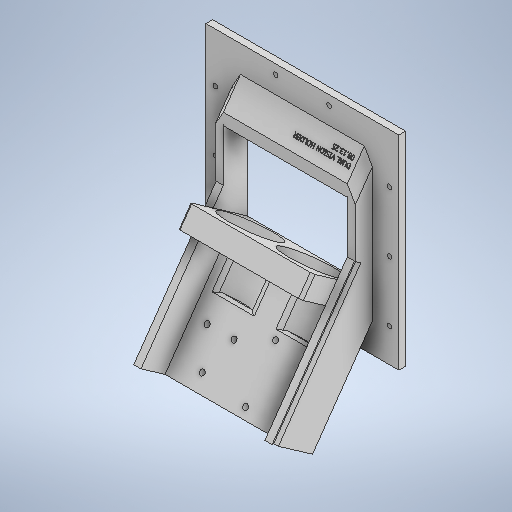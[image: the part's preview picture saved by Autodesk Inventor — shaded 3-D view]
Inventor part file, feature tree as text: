
AUTODESK INVENTOR PART (.ipt)
format: ipt  version: 2025.3 (Build 293356030, 356C)  size: 1,616,896 bytes
history: native  units: in
note: dims shown in document units (in); Inventor stores cm internally (conversion verified against a paired STEP export)
features: sketch x58, extrude x53, projected_geometry x13, plane x5, chamfer x3, move_body x1, hole x1
ambient origin geometry x8: Origin, YZ Plane, XZ Plane, XY Plane, X Axis, Y Axis, Z Axis, Center Point
bodies: Solid1 (feature_tree)
feature tree (134):
  extrude  "Extrusion1"  Depth=0.1969in TaperAngle=0.0deg
  move_body  "Move Body1"
  plane  "Work Plane1"
  sketch  "Sketch5"  dims[d5=1.7717in d6=1.7717in d7=1.7717in d8=1.7717in d9=0.8108in d10=90.0deg d11=0.0787in d12=0.3701in d13=0.4252in d14=0.1362in d15=-0.0984in d16=-0.0591in d17=0.0in]
  plane  "Work Plane2"
  extrude  "Extrusion4"  TaperAngle=0.0deg  [1 undecoded]
  extrude  "Extrusion6"  Depth=0.2405in
  extrude  "Extrusion8"  Depth=2.7559in TaperAngle=0.0deg
  chamfer  "Chamfer1"  [1 undecoded]
  extrude  "Extrusion11"  Depth=0.2362in
  plane  "Work Plane3"
  extrude  "Extrusion13"  Depth=0.1969in TaperAngle=0.0deg
  plane  "Work Plane4"
  plane  "Work Plane6"
  extrude  "Extrusion21"  Depth=0.5027in
  extrude  "Extrusion22"  Depth=0.5027in
  extrude  "Extrusion25"  Depth=1.1811in TaperAngle=0.0deg
  extrude  "Extrusion26"  Depth=0.1969in
  sketch  "Sketch33"  dims[d100=3.6403in d101=2.7717in]
  extrude  "Extrusion27"  Depth=0.2362in TaperAngle=0.0deg
  extrude  "Extrusion29"  Depth=3.6403in
  extrude  "Extrusion28"  Depth=0.6299in TaperAngle=0.0deg
  sketch  "Sketch36"  dims[d124=0.9712in d125=0.0in d126=0.5906in d127=0.0in]
  extrude  "Extrusion30"  Depth=0.7874in
  extrude  "Extrusion31"  Depth=0.5906in TaperAngle=0.0deg
  sketch  "Sketch39"  dims[d164=0.1181in d165=0.0in d168=0.5906in d169=0.0in]
  extrude  "Extrusion35"  Depth=11.3469in TaperAngle=0.0deg
  sketch  "Sketch45"  dims[d176=0.7313in d177=0.0in d186=0.0in d187=0.0in]
  extrude  "Extrusion37"  Depth=0.1181in TaperAngle=0.0deg
  extrude  "Extrusion38"  Depth=0.1181in TaperAngle=0.0deg
  extrude  "Extrusion40"  TaperAngle=0.0deg  [1 undecoded]
  extrude  "Extrusion41"  TaperAngle=0.0deg  [1 undecoded]
  extrude  "Extrusion43"  TaperAngle=0.0deg  [1 undecoded]
  extrude  "Extrusion44"  Depth=0.0394in TaperAngle=0.0deg
  extrude  "Extrusion46"  Depth=3.9671in TaperAngle=0.0deg
  extrude  "Extrusion47"  Depth=0.1969in
  extrude  "Extrusion48"  TaperAngle=60.0deg  [1 undecoded]
  sketch  "Sketch61"  dims[d257=0.1181in d258=0.0in d259=0.0787in d260=0.0in]
  extrude  "Extrusion50"  Depth=0.1969in
  extrude  "Extrusion51"  Depth=0.3937in
  extrude  "Extrusion52"  Depth=0.3937in
  extrude  "Extrusion53"  Depth=0.0787in TaperAngle=0.0deg
  extrude  "Extrusion54"  Depth=0.3937in TaperAngle=0.0deg
  extrude  "Extrusion57"  TaperAngle=0.0deg  [1 undecoded]
  extrude  "Extrusion59"  Depth=0.9449in
  extrude  "Extrusion60"  TaperAngle=0.0deg  [1 undecoded]
  extrude  "Event Cam Hole"  Depth=1.1614in
  extrude  "Extrusion62"  Depth=0.6299in TaperAngle=0.0deg
  extrude  "Extrusion63"  Depth=0.1969in TaperAngle=0.0deg
  extrude  "Extrusion64"  Depth=0.1181in TaperAngle=0.0deg
  extrude  "Extrusion65"  Depth=0.1575in
  extrude  "Extrusion70"  Depth=0.1575in
  extrude  "Extrusion74"  Depth=0.1575in
  extrude  "Extrusion76"  Depth=0.1575in
  extrude  "Extrusion77"  Depth=3.6405in
  extrude  "Extrusion78"  Depth=0.2756in
  extrude  "Extrusion81"  Depth=0.1181in TaperAngle=0.0deg
  chamfer  "Chamfer3"  Distance=0.1956in
  extrude  "Extrusion82"  TaperAngle=0.0deg  [1 undecoded]
  extrude  "Extrusion83"  Depth=0.0787in TaperAngle=45.0deg
  extrude  "Extrusion84"  Depth=0.3543in
  extrude  "Extrusion85"  Depth=0.3543in
  extrude  "Extrusion86"  Depth=0.1181in
  chamfer  "Chamfer4"  Distance=0.0984in
  extrude  "Extrusion87"  TaperAngle=0.0deg  [1 undecoded]
  extrude  "Extrusion88"  Depth=1.0236in TaperAngle=0.0deg
  sketch  "Sketch107"  dims[d398=0.3937in]
  extrude  "Extrusion89"  Depth=0.3937in TaperAngle=0.0deg
  extrude  "Extrusion90"  Depth=0.3937in
  sketch  "Sketch1"  dims[d1=0.5512in d2=0.1969in d3=0.0in]
  sketch  "Sketch6"  dims[d18=0.2749in d24=0.2405in]
  sketch  "Sketch8"  dims[d25=2.7559in d26=0.0in d29=2.5591in d30=0.0in d36=0.0in d37=0.0in]
  sketch  "Sketch12"  dims[d42=0.2362in d43=0.2362in]
  sketch  "Sketch15"  dims[d52=0.2362in d53=0.0787in d54=45.0deg d55=0.1969in d56=0.0in]
  sketch  "Sketch17"  dims[d59=0.5906in d60=0.0in d76=0.5027in]
  sketch  "Sketch27"  dims[d77=0.5027in d78=0.5027in]
  sketch  "Sketch28"  dims[d79=0.5027in d81=1.1811in d82=0.0in]
  sketch  "Sketch31"  dims[d83=0.0in d84=0.0in d91=0.1969in]
  sketch  "Sketch32"  dims[d94=0.2362in d95=0.0in d96=0.2362in d97=0.0in]
  sketch  "Sketch34"  dims[d112=1.9685in d113=0.6299in d114=0.0in]
  sketch  "Sketch35"  dims[d115=0.1575in d117=0.1575in d122=0.7874in d123=0.9331in]
  sketch  "Sketch37"  dims[d128=11.3469in d129=0.0in d130=11.3469in d131=0.0in]
  sketch  "Sketch38"  dims[d141=0.6299in d156=0.1181in d157=0.0in]
  sketch  "Sketch44"  dims[d170=4.7244in d171=0.0in d174=0.0in d175=0.0in]
  projected_geometry  "Projected Loop2"
  projected_geometry  "Projected Loop3"
  projected_geometry  "Projected Loop5"
  sketch  "Sketch47"  dims[d188=0.0in d189=0.0in d194=0.0in d195=0.0in]
  sketch  "Sketch49"  dims[d198=0.0591in d199=0.0in d200=0.0394in d201=0.0in]
  sketch  "Sketch50"  dims[d235=6.1063in d236=0.0in d244=3.9671in d245=0.0in]
  sketch  "Sketch52"  dims[d246=0.9963in d248=0.1969in]
  sketch  "Sketch53"  dims[d249=0.1378in d250=60.0deg]
  sketch  "Sketch56"  dims[d251=0.1969in d252=0.1378in]
  sketch  "Sketch58"  dims[d253=60.0deg d254=0.3937in]
  sketch  "Sketch59"  dims[d255=0.3937in d256=0.3937in]
  sketch  "Sketch63"  dims[d261=1.9685in d262=0.0in d271=0.3937in d272=0.0in]
  sketch  "Sketch64"  dims[d275=0.3937in d276=0.0in d277=0.0in d278=0.0in]
  sketch  "Sketch65"  dims[d279=1.6142in d280=0.9449in]
  sketch  "Sketch66"  dims[d281=1.2598in d282=0.0in d283=0.0in]
  sketch  "Sketch67"  dims[d284=1.5748in d287=1.1614in]
  sketch  "Sketch70"  dims[d288=0.8512in d289=0.6299in d290=0.0in]
  sketch  "Sketch72"  dims[d291=2.9921in d292=0.0in d293=0.1969in d294=0.0in]
  sketch  "Sketch75"  dims[d295=0.1181in d296=0.0in d314=0.0197in d315=0.0in]
  sketch  "Sketch76"  dims[d331=0.3937in d332=0.1575in]
  sketch  "Sketch77"  dims[d333=0.1575in d334=1.0236in]
  sketch  "Sketch79"  dims[d335=0.1575in d336=1.5354in]
  projected_geometry  "Projected Loop11"
  sketch  "Sketch80"  dims[d337=0.1575in d338=1.0236in]
  projected_geometry  "Projected Loop12"
  sketch  "Sketch81"  dims[d339=3.6405in d340=0.0in d347=0.2756in]
  sketch  "Sketch86"  dims[d348=0.2756in d349=0.2756in]
  projected_geometry  "Projected Loop14"
  sketch  "Sketch90"  dims[d351=0.2756in d352=0.1181in d353=0.0in d354=0.1956in d355=0.0in]
  sketch  "Sketch94"  dims[d356=0.0197in d357=0.0in d358=0.0in]
  sketch  "Sketch95"  dims[d363=3.6403in d364=0.0in d365=0.0787in d366=0.0787in d367=45.0deg]
  projected_geometry  "Projected Loop15"
  projected_geometry  "Projected Loop16"
  sketch  "Sketch96"  dims[d371=0.3543in d372=0.3543in]
  sketch  "Sketch99"  dims[d373=0.3543in d374=0.3543in]
  sketch  "Sketch100"  dims[d375=0.1181in d376=0.1181in d377=0.0984in d378=0.0in]
  sketch  "Sketch101"  dims[d379=0.067in d380=0.0in d381=0.0in d382=0.0in]
  projected_geometry  "Projected Loop17"
  sketch  "Sketch102"  dims[d383=1.0236in d384=0.0in d385=1.0236in d386=0.0in]
  projected_geometry  "Projected Loop18"
  sketch  "Sketch103"  dims[d387=0.0787in d388=0.0787in d389=45.0deg d390=0.3937in d391=0.0in]
  projected_geometry  "Projected Loop19"
  sketch  "Sketch104"  dims[d392=0.3937in d393=0.0in d394=0.3937in]
  projected_geometry  "Projected Loop20"
  sketch  "Sketch105"  dims[d395=0.3937in d396=0.3937in]
  sketch  "Sketch106"  dims[d397=0.3937in]
  sketch  "Sketch108"  dims[d399=0.3937in d400=0.3937in d401=0.0787in d402=0.0in d403=0.1181in d404=0.0in d38=0.0197in d39=0.0344in d57=0.0197in d58=0.0344in d158=0.0197in d159=0.0344in d178=0.0in d179=0.0in d180=0.0in d181=0.0in d202=0.0197in d203=0.0344in d359=0.0344in]
  projected_geometry  "Projected Loop21"
  sketch  "Sketch2"  dims[d4=0.315in]
  hole  "Hole1"  [1 undecoded]
note: 11 required parameter values undecoded (feature->parameter linkage not recoverable at this tier; creation-order binding heuristic only, values carry confidence <= 0.55)
